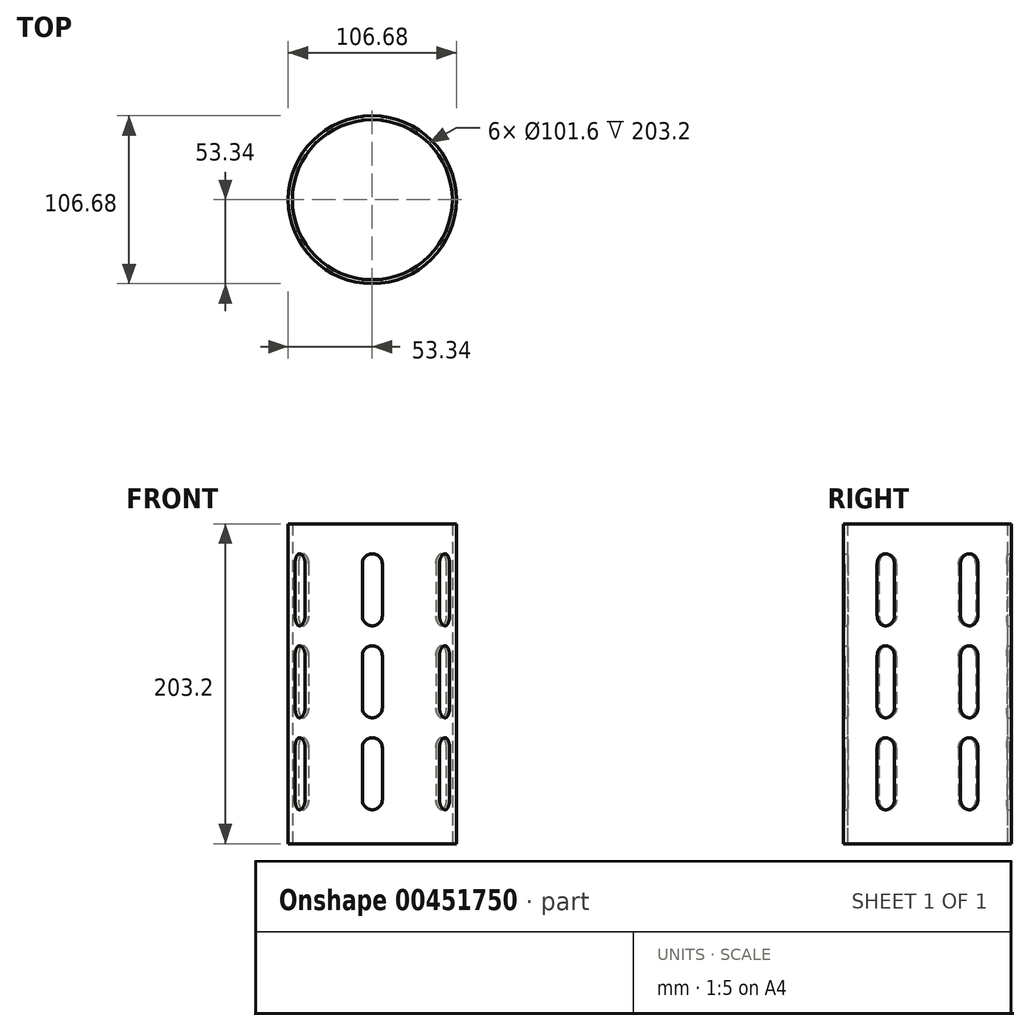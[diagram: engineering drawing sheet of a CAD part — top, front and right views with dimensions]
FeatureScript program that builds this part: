
annotation { "Feature Type Name" : "Feature", "Feature Type Description" : "" }
export const myFeature = defineFeature(function(context is Context, id is Id, definition is map)
    precondition{}
    {
        {
            var Q0;
            Q0=qCreatedBy(makeId("Front.planeOp"),FACE);
            var sketch = newSketch(context, id + "F0", { "sketchPlane" : qUnion([Q0])});
            skLineSegment(sketch, "E0.bottom", {"start": v(50.8, 0) * mm, "end": v(53.34, 0) * mm});
            skLineSegment(sketch, "E0.top", {"start": v(50.8, 203.2) * mm, "end": v(53.34, 203.2) * mm});
            skLineSegment(sketch, "E0.left", {"start": v(50.8, 0) * mm, "end": v(50.8, 203.2) * mm});
            skLineSegment(sketch, "E0.right", {"start": v(53.34, 0) * mm, "end": v(53.34, 203.2) * mm});
            skLineSegment(sketch, "E1", {"start": v(0, 0) * mm, "end": v(0, 32.5) * mm});
            skSolve(sketch);
        }
        {
            var Q0;
            Q0=makeQuery(id+"F0.imprint","IMPRINT",FACE,{"disambiguationData":[TD([[makeQuery(id+"F0.imprint","IMPRINT",EDGE,{"derivedFrom":sQuery(id+"F0.wireOp",EDGE,"E0.bottom")}),1.0]])]});
            var Q1;
            Q1=sQuery(id+"F0.wireOp",EDGE,"E1");
            revolve(context, id + "F1", {"entities" : qUnion([Q0]), "axis" : qUnion([Q1]), "revolveType" : RevolveType.FULL});
        }
        {
            var Q0;
            Q0=qCreatedBy(makeId("Front.planeOp"),FACE);
            var sketch = newSketch(context, id + "F2", { "sketchPlane" : qUnion([Q0])});
            skLineSegment(sketch, "E2", {"start": v(-53.34, 0) * mm, "end": v(-53.34, 203.2) * mm});
            skLineSegment(sketch, "E3", {"start": v(53.34, 203.2) * mm, "end": v(53.34, 0) * mm});
            skArc(sketch, "E4", {"start": v(6.35, 177.8) * mm, "mid": v(0, 184.15) * mm, "end": v(-6.35, 177.8) * mm});
            skArc(sketch, "E5", {"start": v(-6.35, 144.78) * mm, "mid": v(0, 138.43) * mm, "end": v(6.35, 144.78) * mm});
            skLineSegment(sketch, "E6", {"start": v(-6.35, 177.8) * mm, "end": v(-6.35, 144.78) * mm});
            skLineSegment(sketch, "E7", {"start": v(6.35, 177.8) * mm, "end": v(6.35, 144.78) * mm});
            skArc(sketch, "E8", {"start": v(6.35, 119.38) * mm, "mid": v(0, 125.73) * mm, "end": v(-6.35, 119.38) * mm});
            skArc(sketch, "E9", {"start": v(-6.35, 86.36) * mm, "mid": v(0, 80.01) * mm, "end": v(6.35, 86.36) * mm});
            skLineSegment(sketch, "E10", {"start": v(-6.35, 119.38) * mm, "end": v(-6.35, 86.36) * mm});
            skLineSegment(sketch, "E11", {"start": v(6.35, 119.38) * mm, "end": v(6.35, 86.36) * mm});
            skArc(sketch, "E12", {"start": v(6.35, 60.96) * mm, "mid": v(0, 67.3) * mm, "end": v(-6.35, 60.96) * mm});
            skArc(sketch, "E13", {"start": v(-6.35, 27.94) * mm, "mid": v(0, 21.59) * mm, "end": v(6.35, 27.94) * mm});
            skLineSegment(sketch, "E14", {"start": v(-6.35, 60.96) * mm, "end": v(-6.35, 27.94) * mm});
            skLineSegment(sketch, "E15", {"start": v(6.35, 60.96) * mm, "end": v(6.35, 27.94) * mm});
            skSolve(sketch);
        }
        {
            var Q0;
            Q0=makeQuery(id+"F2.imprint","IMPRINT",FACE,{"disambiguationData":[TD([[makeQuery(id+"F2.imprint","IMPRINT",EDGE,{"derivedFrom":sQuery(id+"F2.wireOp",EDGE,"E4")}),1.0]])]});
            var Q1;
            Q1=makeQuery(id+"F2.imprint","IMPRINT",FACE,{"disambiguationData":[TD([[makeQuery(id+"F2.imprint","IMPRINT",EDGE,{"derivedFrom":sQuery(id+"F2.wireOp",EDGE,"E8")}),1.0]])]});
            var Q2;
            Q2=makeQuery(id+"F2.imprint","IMPRINT",FACE,{"disambiguationData":[TD([[makeQuery(id+"F2.imprint","IMPRINT",EDGE,{"derivedFrom":sQuery(id+"F2.wireOp",EDGE,"E12")}),1.0]])]});
            extrude(context, id + "F3", {"entities" : qUnion([Q0, Q1, Q2]), "operationType" : NewBodyOperationType.REMOVE, "endBound" : BoundingType.SYMMETRIC, "oppositeDirection" : true, "depth" : 127 * mm});
        }
        {
            var Q0;
            Q0=makeQuery(id+"F1.opRevolve","SWEPT_BODY",BODY,{"disambiguationData":[OSD([sQuery(id+"F0.wireOp",EDGE,"E0.bottom"),sQuery(id+"F0.wireOp",EDGE,"E0.top"),sQuery(id+"F0.wireOp",EDGE,"E0.left"),sQuery(id+"F0.wireOp",EDGE,"E0.right")])]});
            var Q1;
            Q1=makeQuery(id+"F1.opRevolve","SWEPT_EDGE",EDGE,{"disambiguationData":[OSD([sQuery(id+"F0.wireOp",EDGE,"E0.top"),sQuery(id+"F0.wireOp",EDGE,"E0.left")])]});
            circularPattern(context, id + "F4", {"entities" : qUnion([Q0]), "axis" : qUnion([Q1]), "angle" : 360 * degree, "instanceCount" : 6, "equalSpace" : true});
        }
    });
